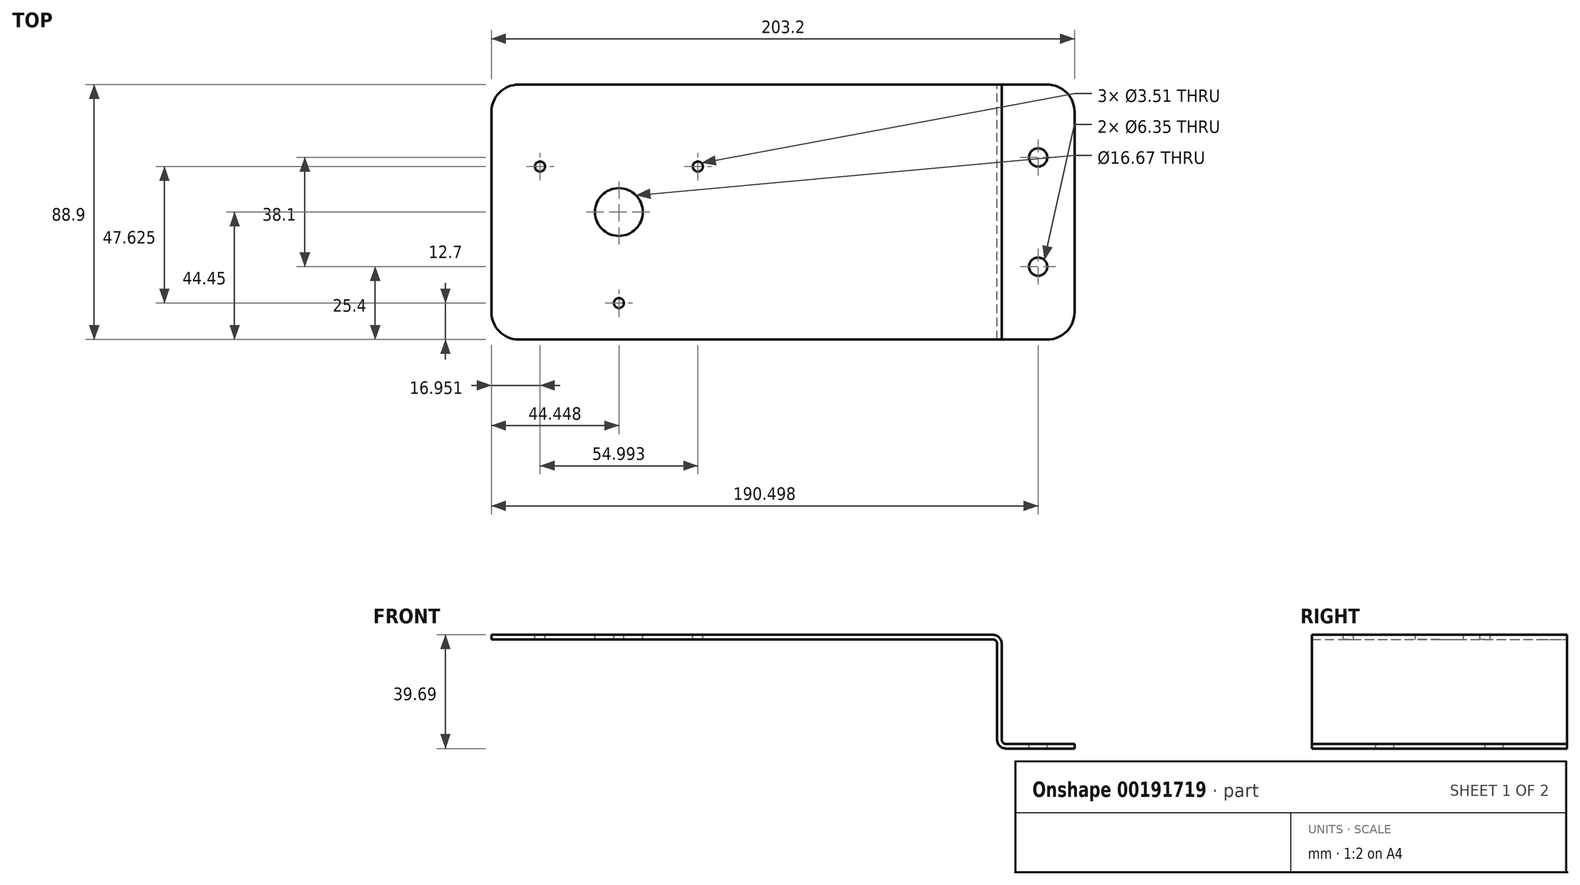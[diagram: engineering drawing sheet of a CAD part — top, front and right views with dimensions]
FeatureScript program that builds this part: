
annotation { "Feature Type Name" : "Feature", "Feature Type Description" : "" }
export const myFeature = defineFeature(function(context is Context, id is Id, definition is map)
    precondition{}
    {
        {
            var Q0;
            Q0=qCreatedBy(makeId("Front.planeOp"),FACE);
            var sketch = newSketch(context, id + "F0", { "sketchPlane" : qUnion([Q0])});
            skLineSegment(sketch, "E0", {"start": v(-1.59, 0) * mm, "end": v(-176.21, 0) * mm});
            skLineSegment(sketch, "E1", {"start": v(0, -1.59) * mm, "end": v(0, -34.93) * mm});
            skPoint(sketch, "E2.visualSharp", {"position": v(0, 0) * mm});
            skArc(sketch, "E2.filletArc", {"start": v(0, -1.59) * mm, "mid": v(-0.46, -0.46) * mm, "end": v(-1.59, 0) * mm});
            skLineSegment(sketch, "E3.0", {"start": v(-1.59, 1.59) * mm, "end": v(-176.21, 1.59) * mm});
            skArc(sketch, "E3.1", {"start": v(1.59, -1.59) * mm, "mid": v(0.66, 0.66) * mm, "end": v(-1.59, 1.59) * mm});
            skLineSegment(sketch, "E3.2", {"start": v(1.59, -1.59) * mm, "end": v(1.59, -34.92) * mm});
            skLineSegment(sketch, "E4", {"start": v(-176.21, 1.59) * mm, "end": v(-176.21, 0) * mm});
            skLineSegment(sketch, "E5", {"start": v(3.18, -36.51) * mm, "end": v(26.99, -36.51) * mm});
            skPoint(sketch, "E6.visualSharp", {"position": v(1.59, -36.51) * mm});
            skArc(sketch, "E6.filletArc", {"start": v(1.59, -34.92) * mm, "mid": v(2.05, -36.05) * mm, "end": v(3.18, -36.51) * mm});
            skLineSegment(sketch, "E7.0", {"start": v(3.18, -38.1) * mm, "end": v(26.99, -38.1) * mm});
            skArc(sketch, "E7.1", {"start": v(0, -34.93) * mm, "mid": v(0.93, -37.17) * mm, "end": v(3.18, -38.1) * mm});
            skLineSegment(sketch, "E8", {"start": v(26.99, -36.51) * mm, "end": v(26.99, -38.1) * mm});
            skSolve(sketch);
        }
        {
            var Q0;
            Q0 = qSketchRegion(id + "F0", true);
            extrude(context, id + "F1", {"entities" : qUnion([Q0]), "endBound" : BoundingType.SYMMETRIC, "depth" : 88.9 * mm});
        }
        {
            var Q0;
            Q0=makeQuery(id+"F1.opExtrude","SWEPT_FACE",FACE,{"disambiguationData":[OSD([sQuery(id+"F0.wireOp",EDGE,"E3.0")])]});
            var sketch = newSketch(context, id + "F2", { "sketchPlane" : qUnion([Q0])});
            skCircle(sketch, "E9", {"center": v(-131.76, 0) * mm, "radius": 8.33 * mm});
            skCircle(sketch, "E10", {"center": v(14.29, 19.05) * mm, "radius": 3.18 * mm});
            skCircle(sketch, "E11", {"center": v(14.29, -19.05) * mm, "radius": 3.18 * mm});
            skCircle(sketch, "E12", {"center": v(-131.76, 0) * mm, "radius": 31.75 * mm, "construction": true});
            skCircle(sketch, "E13", {"center": v(-131.76, -31.75) * mm, "radius": 1.75 * mm});
            skCircle(sketch, "E14.1.0", {"center": v(-104.27, 15.87) * mm, "radius": 1.75 * mm});
            skCircle(sketch, "E14.2.0", {"center": v(-159.26, 15.88) * mm, "radius": 1.75 * mm});
            skSolve(sketch);
        }
        {
            var Q0;
            Q0 = qSketchRegion(id + "F2", true);
            extrude(context, id + "F3", {"entities" : qUnion([Q0]), "operationType" : NewBodyOperationType.REMOVE, "endBound" : BoundingType.THROUGH_ALL, "oppositeDirection" : true, "depth" : 25.4 * mm});
        }
        {
            var Q0;
            Q0=makeQuery(id+"F1.opExtrude","CAP_EDGE",EDGE,{"disambiguationData":[OSD([sQuery(id+"F0.wireOp",EDGE,"E4")])],"isStart":false});
            var Q1;
            Q1=makeQuery(id+"F1.opExtrude","CAP_EDGE",EDGE,{"disambiguationData":[OSD([sQuery(id+"F0.wireOp",EDGE,"E4")])],"isStart":true});
            var Q2;
            Q2=makeQuery(id+"F1.opExtrude","CAP_EDGE",EDGE,{"disambiguationData":[OSD([sQuery(id+"F0.wireOp",EDGE,"E8")])],"isStart":true});
            var Q3;
            Q3=makeQuery(id+"F1.opExtrude","CAP_EDGE",EDGE,{"disambiguationData":[OSD([sQuery(id+"F0.wireOp",EDGE,"E8")])],"isStart":false});
            fillet(context, id + "F4", {"entities" : qUnion([Q0, Q1, Q2, Q3]), "radius" : 9.52 * mm, "tangentPropagation" : true, "allowEdgeOverflow" : false});
        }
    });
